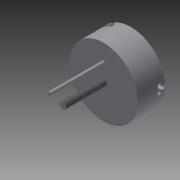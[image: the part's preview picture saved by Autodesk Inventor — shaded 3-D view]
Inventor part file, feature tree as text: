
AUTODESK INVENTOR PART (.ipt)
format: ipt  version: 2015 (Build 190159000, 159)  size: 160,256 bytes
history: native  units: mm
features: extrude x7, sketch x7, thread x1
ambient origin geometry x8: Origin, YZ Plane, XZ Plane, XY Plane, X Axis, Y Axis, Z Axis, Center Point
bodies: Solid1 (feature_tree)
feature tree (15):
  extrude  "Extrusion1"  Depth=40.0mm TaperAngle=0.0deg
  extrude  "Extrusion6"  Depth=60.0mm TaperAngle=0.0deg
  thread  "Thread1"  [1 undecoded]
  extrude  "Extrusion7"  Depth=5.0mm
  extrude  "Extrusion8"  Depth=5.0mm
  extrude  "Extrusion9"  Depth=5.0mm
  extrude  "Extrusion10"  Depth=15.0mm
  extrude  "Extrusion11"  Depth=5.0mm
  sketch  "Sketch1"  dims[d0=100.0mm d1=40.0mm d2=0.0mm]
  sketch  "Sketch6"  dims[d36=10.0mm d37=60.0mm d38=0.0mm d39=10.0mm d40=0.0mm]
  sketch  "Sketch7"  dims[d52=5.0mm d55=6.0mm]
  sketch  "Sketch8"  dims[d58=2.5mm d60=5.0mm]
  sketch  "Sketch9"  dims[d61=5.0mm d62=0.0mm d63=5.0mm]
  sketch  "Sketch10"  dims[d64=5.0mm d65=15.0mm]
  sketch  "Sketch11"  dims[d66=60.0mm d67=0.0mm d68=5.0mm d69=5.0mm d70=15.0mm d71=60.0mm d72=0.0mm d73=5.0mm d74=5.0mm d75=15.0mm d76=60.0mm d77=0.0mm d80=80.0mm d81=0.0mm d82=5.0mm]
note: 1 required parameter value undecoded (feature->parameter linkage not recoverable at this tier; creation-order binding heuristic only, values carry confidence <= 0.55)
